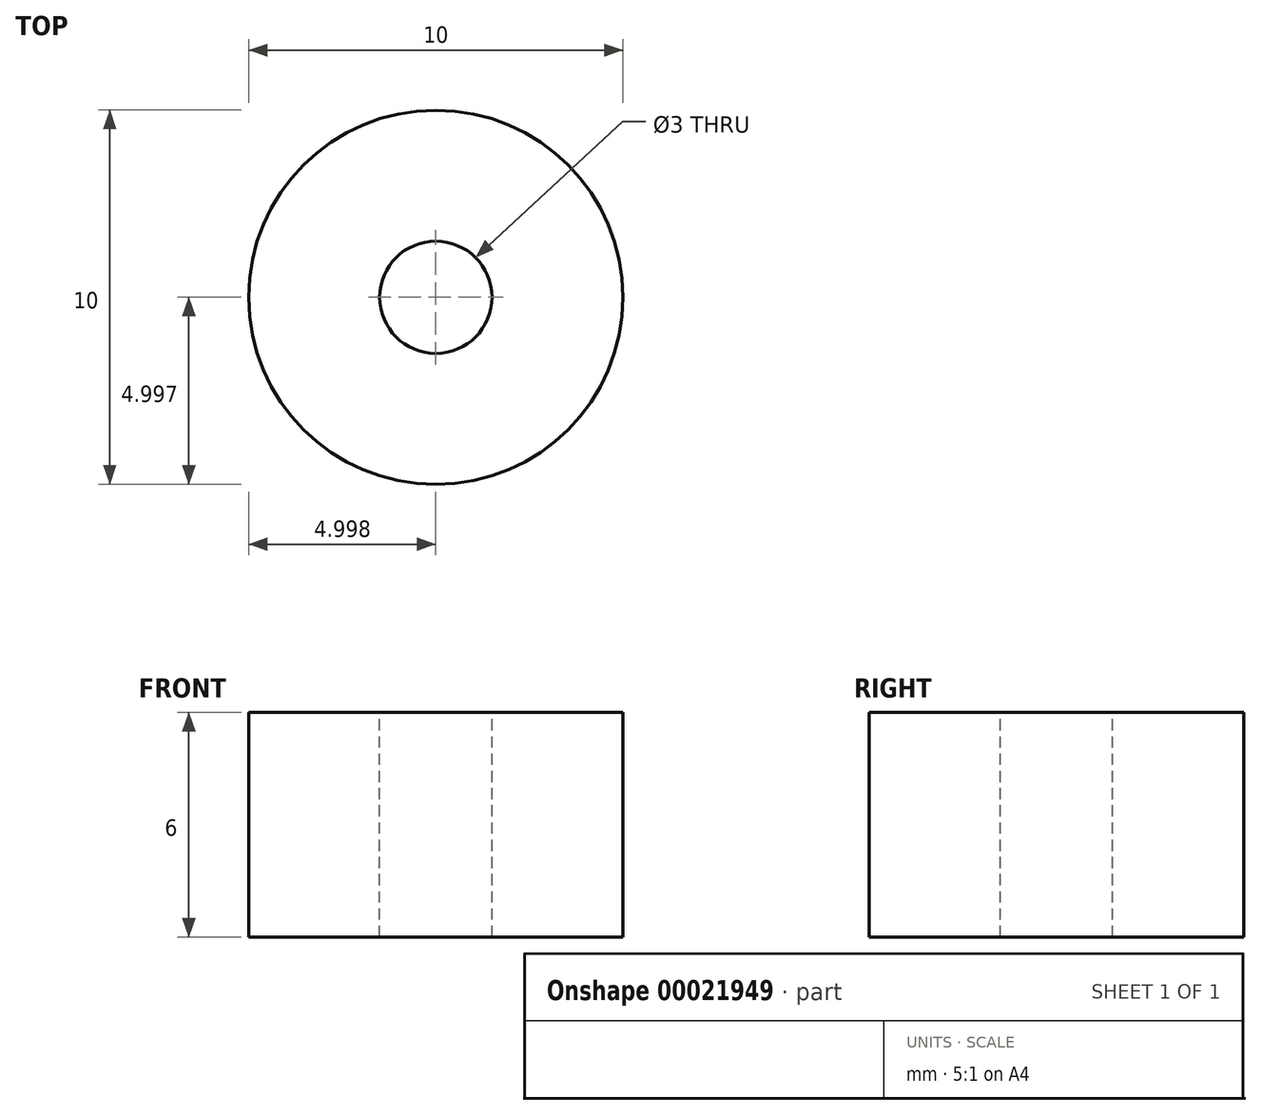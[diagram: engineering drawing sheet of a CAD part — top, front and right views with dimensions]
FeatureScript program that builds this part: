
annotation { "Feature Type Name" : "Feature", "Feature Type Description" : "" }
export const myFeature = defineFeature(function(context is Context, id is Id, definition is map)
    precondition{}
    {
        {
            var Q0;
            Q0=qCreatedBy(makeId("Top.planeOp"),FACE);
            var sketch = newSketch(context, id + "F0", { "sketchPlane" : qUnion([Q0])});
            skCircle(sketch, "E0", {"center": v(-11.4, -3.76) * mm, "radius": 5 * mm});
            skSolve(sketch);
        }
        {
            var Q0;
            Q0 = qSketchRegion(id + "F0", true);
            var Q1;
            Q1=makeQuery(id+"F0.imprint","IMPRINT",FACE,{"disambiguationData":[TD([[makeQuery(id+"F0.imprint","IMPRINT",EDGE,{"derivedFrom":sQuery(id+"F0.wireOp",EDGE,"E0")}),1.0]])]});
            extrude(context, id + "F1", {"entities" : qUnion([Q0, Q1]), "depth" : 6 * mm});
        }
        {
            var Q0;
            Q0=makeQuery(id+"F1.opExtrude","CAP_FACE",FACE,{"disambiguationData":[OSD([sQuery(id+"F0.wireOp",EDGE,"E0")])],"isStart":false});
            var sketch = newSketch(context, id + "F2", { "sketchPlane" : qUnion([Q0])});
            skCircle(sketch, "E1", {"center": v(-11.4, -3.76) * mm, "radius": 1.5 * mm});
            skSolve(sketch);
        }
        {
            var Q0;
            Q0 = qSketchRegion(id + "F2", true);
            extrude(context, id + "F3", {"entities" : qUnion([Q0]), "operationType" : NewBodyOperationType.REMOVE, "oppositeDirection" : true, "depth" : 25 * mm});
        }
    });
